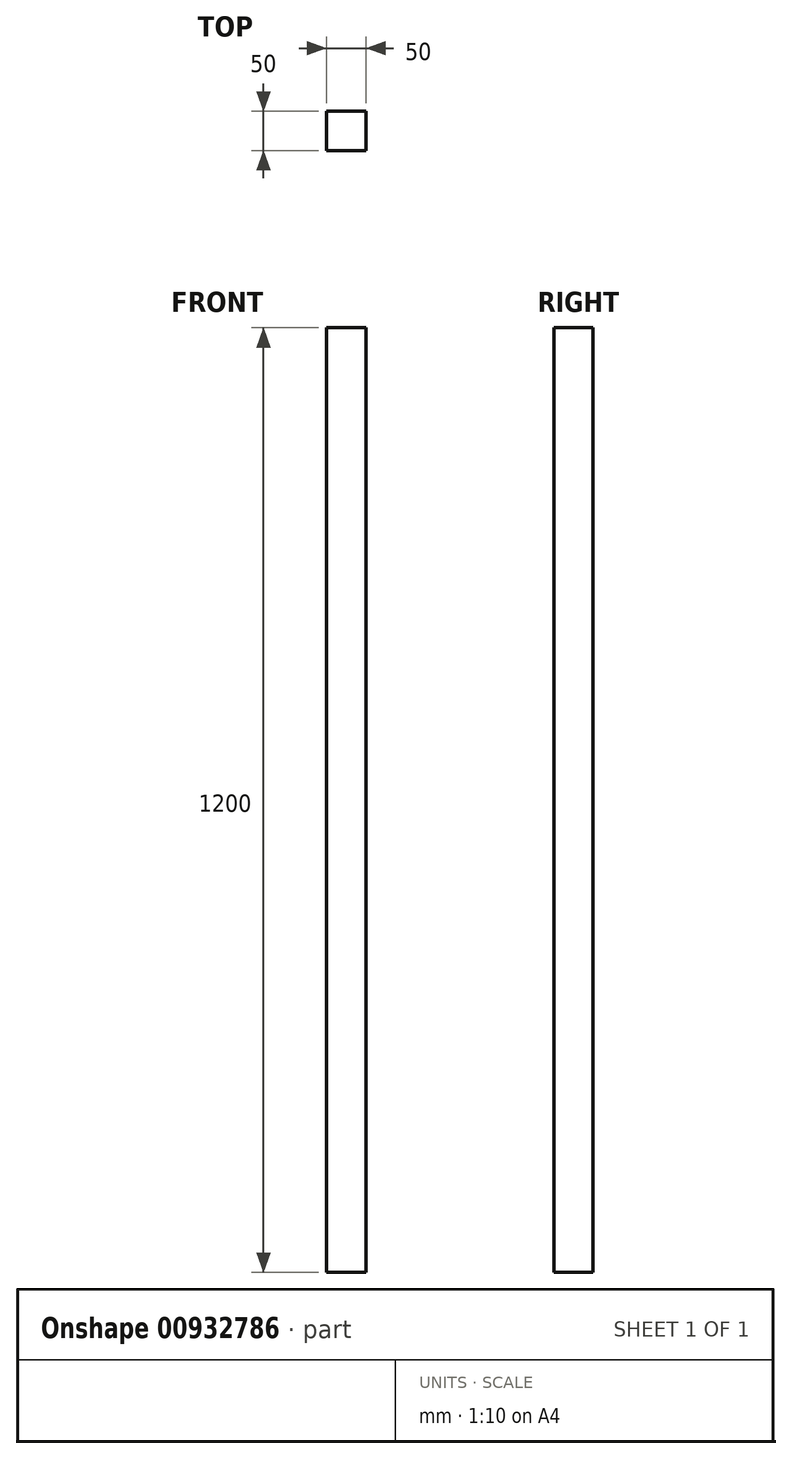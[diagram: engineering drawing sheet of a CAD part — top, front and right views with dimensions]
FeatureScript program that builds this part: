
annotation { "Feature Type Name" : "Feature", "Feature Type Description" : "" }
export const myFeature = defineFeature(function(context is Context, id is Id, definition is map)
    precondition{}
    {
        {
            var Q0;
            Q0=qCreatedBy(makeId("Top.planeOp"),FACE);
            var sketch = newSketch(context, id + "F0", { "sketchPlane" : qUnion([Q0])});
            skLineSegment(sketch, "E0.bottom", {"start": v(-73.01, -38.1) * mm, "end": v(-23.01, -38.1) * mm});
            skLineSegment(sketch, "E0.top", {"start": v(-73.01, -88.1) * mm, "end": v(-23.01, -88.1) * mm});
            skLineSegment(sketch, "E0.left", {"start": v(-73.01, -38.1) * mm, "end": v(-73.01, -88.1) * mm});
            skLineSegment(sketch, "E0.right", {"start": v(-23.01, -38.1) * mm, "end": v(-23.01, -88.1) * mm});
            skSolve(sketch);
        }
        {
            var Q0;
            Q0=makeQuery(id+"F0.imprint","IMPRINT",FACE,{"disambiguationData":[TD([[makeQuery(id+"F0.imprint","IMPRINT",EDGE,{"derivedFrom":sQuery(id+"F0.wireOp",EDGE,"E0.bottom")}),-1.0]])]});
            extrude(context, id + "F1", {"entities" : qUnion([Q0]), "depth" : 1200 * mm, "offsetDistance" : 25 * mm});
        }
    });
